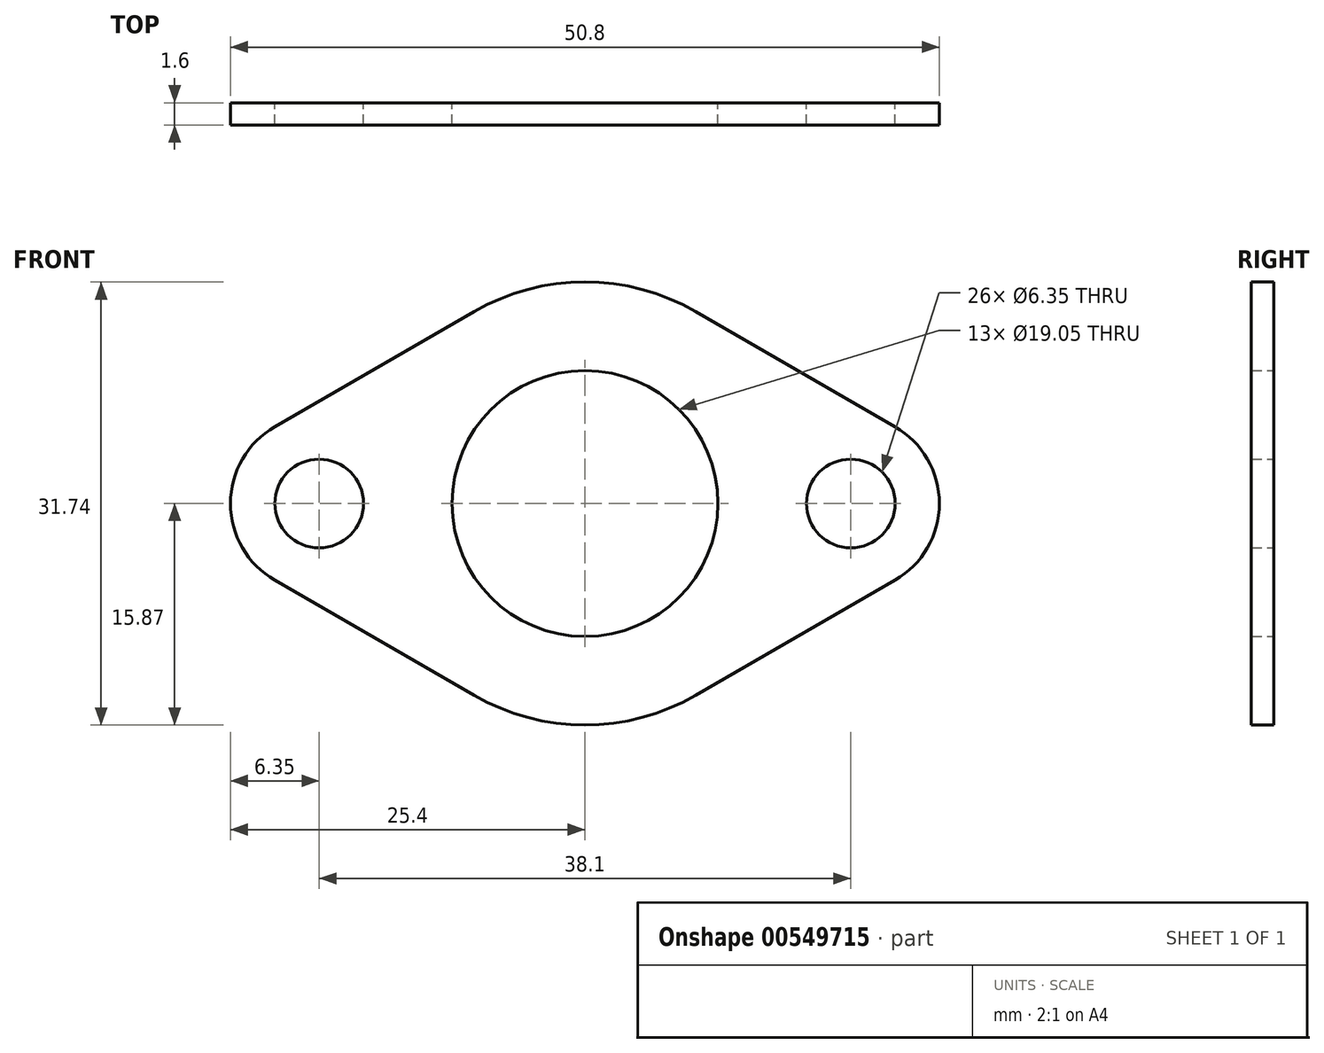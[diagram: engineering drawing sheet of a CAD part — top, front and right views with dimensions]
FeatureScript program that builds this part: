
annotation { "Feature Type Name" : "Feature", "Feature Type Description" : "" }
export const myFeature = defineFeature(function(context is Context, id is Id, definition is map)
    precondition{}
    {
        {
            var Q0;
            Q0=qCreatedBy(makeId("Front.planeOp"),FACE);
            var sketch = newSketch(context, id + "F0", { "sketchPlane" : qUnion([Q0])});
            skCircle(sketch, "E0", {"center": v(-19.05, 0) * mm, "radius": 3.18 * mm});
            skCircle(sketch, "E1", {"center": v(19.05, 0) * mm, "radius": 3.18 * mm});
            skCircle(sketch, "E2", {"center": v(0, 0) * mm, "radius": 9.53 * mm});
            skArc(sketch, "E3", {"start": v(-22.22, 5.5) * mm, "mid": v(-25.4, 0) * mm, "end": v(-22.23, -5.5) * mm});
            skArc(sketch, "E4", {"start": v(22.23, -5.5) * mm, "mid": v(25.4, 0) * mm, "end": v(22.23, 5.5) * mm});
            skArc(sketch, "E5", {"start": v(-7.94, -13.75) * mm, "mid": v(0, -15.88) * mm, "end": v(7.94, -13.75) * mm});
            skArc(sketch, "E6.trimOffspring", {"start": v(7.94, 13.75) * mm, "mid": v(0, 15.88) * mm, "end": v(-7.94, 13.75) * mm});
            skLineSegment(sketch, "E7", {"start": v(-22.23, 5.5) * mm, "end": v(-7.94, 13.75) * mm});
            skLineSegment(sketch, "E8", {"start": v(22.23, 5.5) * mm, "end": v(7.94, 13.75) * mm});
            skLineSegment(sketch, "E9", {"start": v(-22.22, -5.5) * mm, "end": v(-7.94, -13.75) * mm});
            skLineSegment(sketch, "E10", {"start": v(22.23, -5.5) * mm, "end": v(7.94, -13.75) * mm});
            skSolve(sketch);
        }
        {
            var Q0;
            Q0=makeQuery(id+"F0.imprint","IMPRINT",FACE,{"disambiguationData":[TD([[makeQuery(id+"F0.imprint","IMPRINT",EDGE,{"derivedFrom":sQuery(id+"F0.wireOp",EDGE,"E0")}),-1.0]])]});
            extrude(context, id + "F1", {"entities" : qUnion([Q0]), "depth" : 1.6 * mm, "offsetDistance" : 25.4 * mm});
        }
    });
